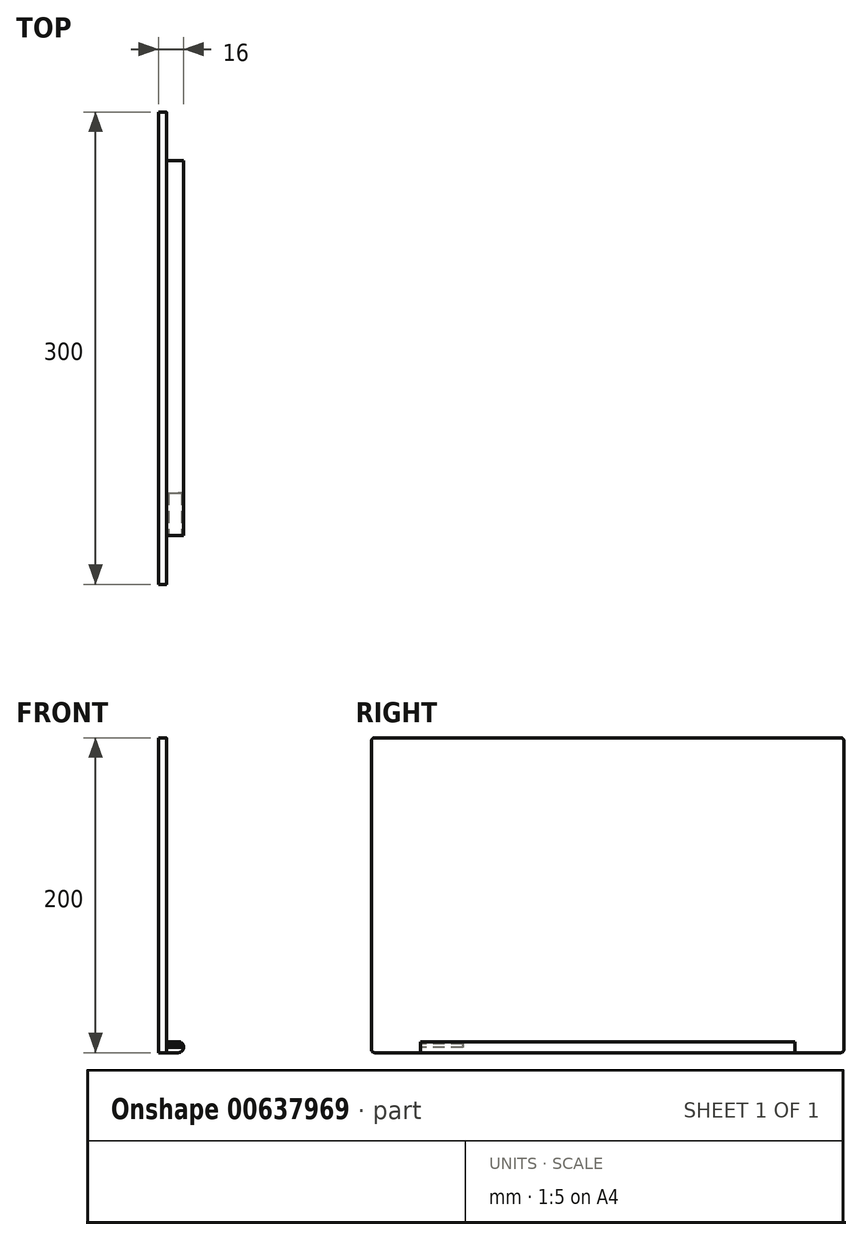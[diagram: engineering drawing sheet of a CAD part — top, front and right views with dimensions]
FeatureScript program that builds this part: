
annotation { "Feature Type Name" : "Feature", "Feature Type Description" : "" }
export const myFeature = defineFeature(function(context is Context, id is Id, definition is map)
    precondition{}
    {
        {
            var Q0;
            Q0=qCreatedBy(makeId("Front.planeOp"),FACE);
            var sketch = newSketch(context, id + "F0", { "sketchPlane" : qUnion([Q0])});
            skLineSegment(sketch, "E0", {"start": v(0, 0) * mm, "end": v(0, 200) * mm});
            skLineSegment(sketch, "E1", {"start": v(0, 200) * mm, "end": v(5, 200) * mm});
            skLineSegment(sketch, "E2", {"start": v(5, 200) * mm, "end": v(5, 0) * mm});
            skLineSegment(sketch, "E3", {"start": v(5, 0) * mm, "end": v(0, 0) * mm});
            skSolve(sketch);
        }
        {
            var Q0;
            Q0=makeQuery(id+"F0.imprint","IMPRINT",FACE,{"disambiguationData":[TD([[makeQuery(id+"F0.imprint","IMPRINT",EDGE,{"derivedFrom":sQuery(id+"F0.wireOp",EDGE,"E0")}),-1.0]])]});
            extrude(context, id + "F1", {"entities" : qUnion([Q0]), "depth" : 300 * mm, "offsetDistance" : 25 * mm});
        }
        {
            var Q0;
            Q0=makeQuery(id+"F1.opExtrude","CAP_FACE",FACE,{"disambiguationData":[OSD([sQuery(id+"F0.wireOp",EDGE,"E0"),sQuery(id+"F0.wireOp",EDGE,"E1"),sQuery(id+"F0.wireOp",EDGE,"E2"),sQuery(id+"F0.wireOp",EDGE,"E3")])],"isStart":false});
            var sketch = newSketch(context, id + "F2", { "sketchPlane" : qUnion([Q0])});
            skLineSegment(sketch, "E4.bottom", {"start": v(5, 0) * mm, "end": v(16, 0) * mm});
            skLineSegment(sketch, "E4.top", {"start": v(5, 7) * mm, "end": v(16, 7) * mm});
            skLineSegment(sketch, "E4.left", {"start": v(5, 0) * mm, "end": v(5, 7) * mm});
            skLineSegment(sketch, "E4.right", {"start": v(16, 0) * mm, "end": v(16, 7) * mm});
            skSolve(sketch);
        }
        {
            var Q0;
            Q0 = qSketchRegion(id + "F2", true);
            extrude(context, id + "F3", {"entities" : qUnion([Q0]), "operationType" : NewBodyOperationType.ADD, "oppositeDirection" : true, "depth" : 300 * mm, "offsetDistance" : 25 * mm});
        }
        {
            var Q0;
            Q0=makeQuery(id+"F3.opExtrude","SWEPT_EDGE",EDGE,{"disambiguationData":[OSD([sQuery(id+"F2.wireOp",EDGE,"E4.top"),sQuery(id+"F2.wireOp",EDGE,"E4.right")])]});
            var Q1;
            Q1=makeQuery(id+"F3.opExtrude","SWEPT_EDGE",EDGE,{"disambiguationData":[OSD([sQuery(id+"F2.wireOp",EDGE,"E4.bottom"),sQuery(id+"F2.wireOp",EDGE,"E4.right")])]});
            fillet(context, id + "F4", {"entities" : qUnion([Q0, Q1]), "radius" : 3.5 * mm, "tangentPropagation" : true, "allowEdgeOverflow" : false});
        }
        {
            var Q0;
            Q0=makeQuery(id+"F3.opExtrude","SWEPT_FACE",FACE,{"disambiguationData":[OSD([sQuery(id+"F2.wireOp",EDGE,"E4.top")])]});
            var sketch = newSketch(context, id + "F5", { "sketchPlane" : qUnion([Q0])});
            skLineSegment(sketch, "E5.bottom", {"start": v(5, -300) * mm, "end": v(20, -300) * mm});
            skLineSegment(sketch, "E5.top", {"start": v(5, -269) * mm, "end": v(20, -269) * mm});
            skLineSegment(sketch, "E5.left", {"start": v(5, -300) * mm, "end": v(5, -269) * mm});
            skLineSegment(sketch, "E5.right", {"start": v(20, -300) * mm, "end": v(20, -269) * mm});
            skLineSegment(sketch, "E6.bottom", {"start": v(5, 0) * mm, "end": v(20, 0) * mm});
            skLineSegment(sketch, "E6.top", {"start": v(5, -31) * mm, "end": v(20, -31) * mm});
            skLineSegment(sketch, "E6.left", {"start": v(5, 0) * mm, "end": v(5, -31) * mm});
            skLineSegment(sketch, "E6.right", {"start": v(20, 0) * mm, "end": v(20, -31) * mm});
            skSolve(sketch);
        }
        {
            var Q0;
            Q0 = qSketchRegion(id + "F5", true);
            extrude(context, id + "F6", {"entities" : qUnion([Q0]), "operationType" : NewBodyOperationType.REMOVE, "endBound" : BoundingType.THROUGH_ALL, "oppositeDirection" : true, "depth" : 25 * mm, "offsetDistance" : 25 * mm});
        }
        {
            var Q0;
            Q0=makeQuery(id+"F1.opExtrude","CAP_EDGE",EDGE,{"disambiguationData":[OSD([sQuery(id+"F0.wireOp",EDGE,"E1")])],"isStart":false});
            var Q1;
            Q1=makeQuery(id+"F1.opExtrude","CAP_EDGE",EDGE,{"disambiguationData":[OSD([sQuery(id+"F0.wireOp",EDGE,"E1")])],"isStart":true});
            var Q2;
            Q2=makeQuery(id+"F3.boolean.opBoolean","MERGE",EDGE,{"derivedFrom":[makeQuery(id+"F1.opExtrude","CAP_EDGE",EDGE,{"disambiguationData":[OSD([sQuery(id+"F0.wireOp",EDGE,"E3")])],"isStart":false}),makeQuery(id+"F3.opExtrude","CAP_EDGE",EDGE,{"disambiguationData":[OSD([sQuery(id+"F2.wireOp",EDGE,"E4.bottom")])],"isStart":true})]});
            var Q3;
            Q3=makeQuery(id+"F3.boolean.opBoolean","MERGE",EDGE,{"derivedFrom":[makeQuery(id+"F1.opExtrude","CAP_EDGE",EDGE,{"disambiguationData":[OSD([sQuery(id+"F0.wireOp",EDGE,"E3")])],"isStart":true}),makeQuery(id+"F3.opExtrude","CAP_EDGE",EDGE,{"disambiguationData":[OSD([sQuery(id+"F2.wireOp",EDGE,"E4.bottom")])],"isStart":false})]});
            fillet(context, id + "F7", {"entities" : qUnion([Q0, Q1, Q2, Q3]), "radius" : 2 * mm, "tangentPropagation" : true, "allowEdgeOverflow" : false});
        }
        {
            var Q0;
            Q0=makeQuery(id+"F6.boolean.opBoolean","COPY",FACE,{"derivedFrom":makeQuery(id+"F6.opExtrude","SWEPT_FACE",FACE,{"disambiguationData":[OSD([sQuery(id+"F5.wireOp",EDGE,"E5.top")])]})});
            var sketch = newSketch(context, id + "F8", { "sketchPlane" : qUnion([Q0])});
            skLineSegment(sketch, "E7", {"start": v(5, 7) * mm, "end": v(6.5, 7) * mm, "construction": true});
            skLineSegment(sketch, "E8", {"start": v(6.5, 7) * mm, "end": v(6.5, 5.5) * mm, "construction": true});
            skPoint(sketch, "E9.oppositeSnap0", {"position": v(16, 3.5) * mm});
            skLineSegment(sketch, "E9.bottom", {"start": v(6.5, 5.5) * mm, "end": v(14.5, 5.5) * mm});
            skLineSegment(sketch, "E9.top", {"start": v(6.5, 3.5) * mm, "end": v(14.5, 3.5) * mm});
            skLineSegment(sketch, "E9.left", {"start": v(6.5, 5.5) * mm, "end": v(6.5, 3.5) * mm});
            skLineSegment(sketch, "E9.right", {"start": v(14.5, 5.5) * mm, "end": v(14.5, 3.5) * mm});
            skSolve(sketch);
        }
        {
            var Q0;
            Q0 = qSketchRegion(id + "F8", true);
            extrude(context, id + "F9", {"entities" : qUnion([Q0]), "operationType" : NewBodyOperationType.REMOVE, "oppositeDirection" : true, "depth" : 27 * mm, "offsetDistance" : 25 * mm});
        }
        {
            var Q0;
            Q0=makeQuery(id+"F9.boolean.opBoolean","COPY",EDGE,{"derivedFrom":makeQuery(id+"F9.opExtrude","SWEPT_EDGE",EDGE,{"disambiguationData":[OSD([sQuery(id+"F8.wireOp",EDGE,"E9.bottom"),sQuery(id+"F8.wireOp",EDGE,"E9.right")])]})});
            fillet(context, id + "F10", {"entities" : qUnion([Q0]), "radius" : 2 * mm, "tangentPropagation" : true, "allowEdgeOverflow" : false});
        }
    });
